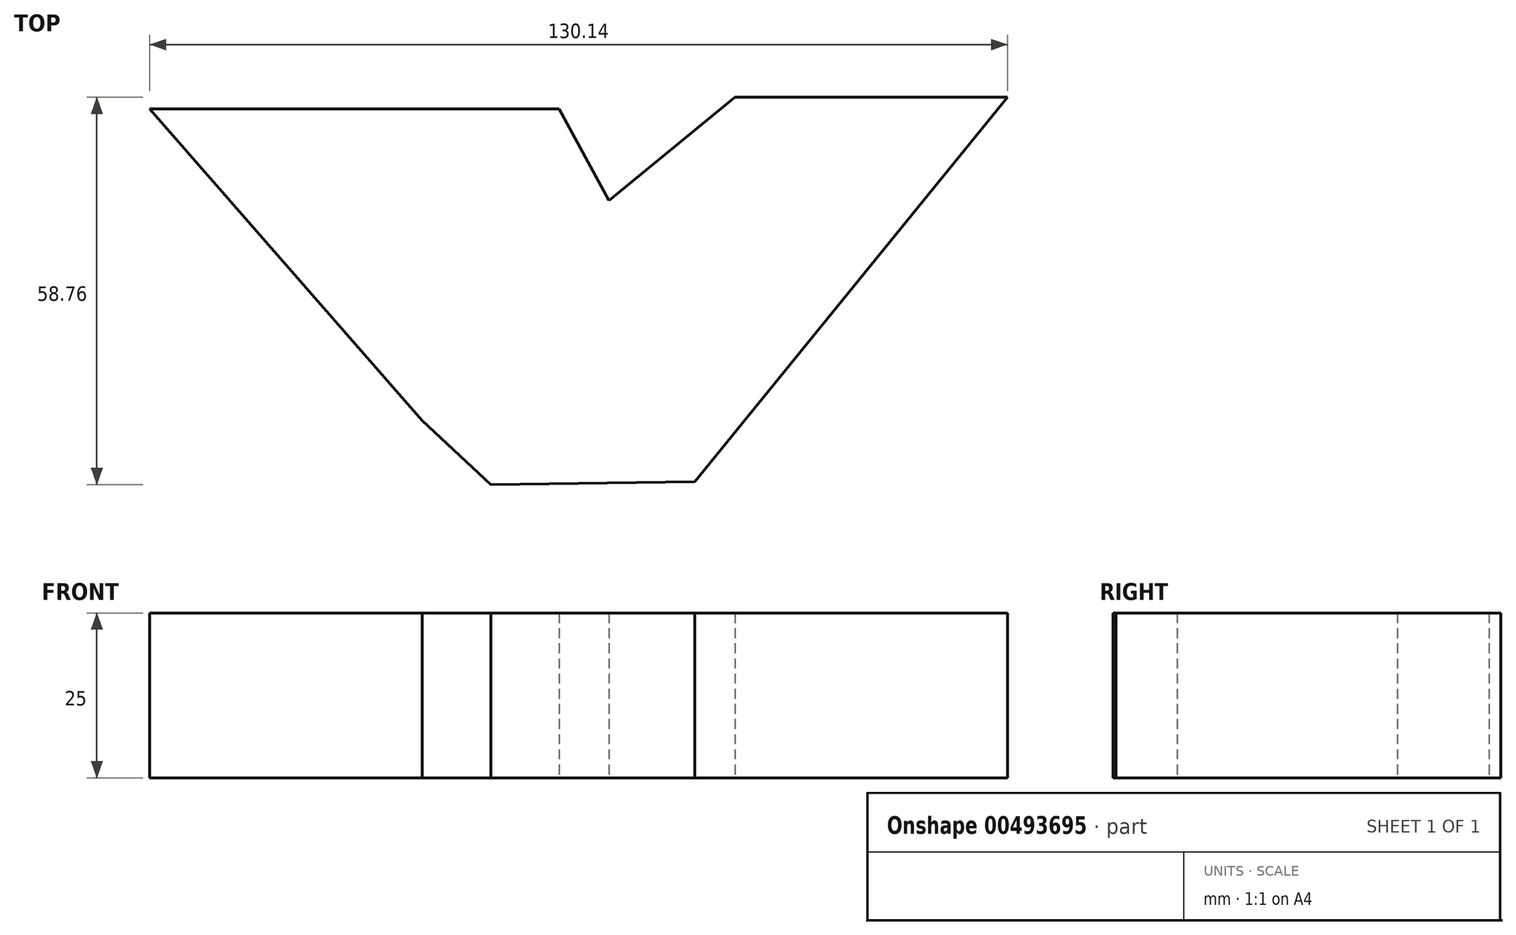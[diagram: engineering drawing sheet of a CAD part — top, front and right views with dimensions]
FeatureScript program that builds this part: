
annotation { "Feature Type Name" : "Feature", "Feature Type Description" : "" }
export const myFeature = defineFeature(function(context is Context, id is Id, definition is map)
    precondition{}
    {
        {
            var Q0;
            Q0=qCreatedBy(makeId("Top.planeOp"),FACE);
            var sketch = newSketch(context, id + "F0", { "sketchPlane" : qUnion([Q0])});
            skLineSegment(sketch, "E0", {"start": v(-62.14, 38.45) * mm, "end": v(0, 38.45) * mm});
            skLineSegment(sketch, "E1", {"start": v(0, 38.45) * mm, "end": v(7.5, 24.52) * mm});
            skLineSegment(sketch, "E2", {"start": v(7.5, 24.52) * mm, "end": v(26.65, 40.19) * mm});
            skLineSegment(sketch, "E3", {"start": v(26.65, 40.19) * mm, "end": v(68, 40.19) * mm});
            skLineSegment(sketch, "E4", {"start": v(-62.14, 38.45) * mm, "end": v(-19.92, -9.87) * mm});
            skLineSegment(sketch, "E5", {"start": v(68, 40.19) * mm, "end": v(20.55, -18.14) * mm});
            skLineSegment(sketch, "E6", {"start": v(-22.54, -7.25) * mm, "end": v(-10.35, -18.57) * mm});
            skLineSegment(sketch, "E7", {"start": v(-10.35, -18.57) * mm, "end": v(20.55, -18.14) * mm});
            skSolve(sketch);
        }
        {
            var Q0;
            {var subQ0=sQuery(id+"F0.wireOp",EDGE,"E0");Q0=makeQuery(id+"F0.imprint","IMPRINT",FACE,{"disambiguationData":[TD([[makeQuery(id+"F0.imprint","IMPRINT",EDGE,{"derivedFrom":subQ0}),-1.0]])]});}
            extrude(context, id + "F1", {"entities" : qUnion([Q0]), "depth" : 25 * mm});
        }
    });
